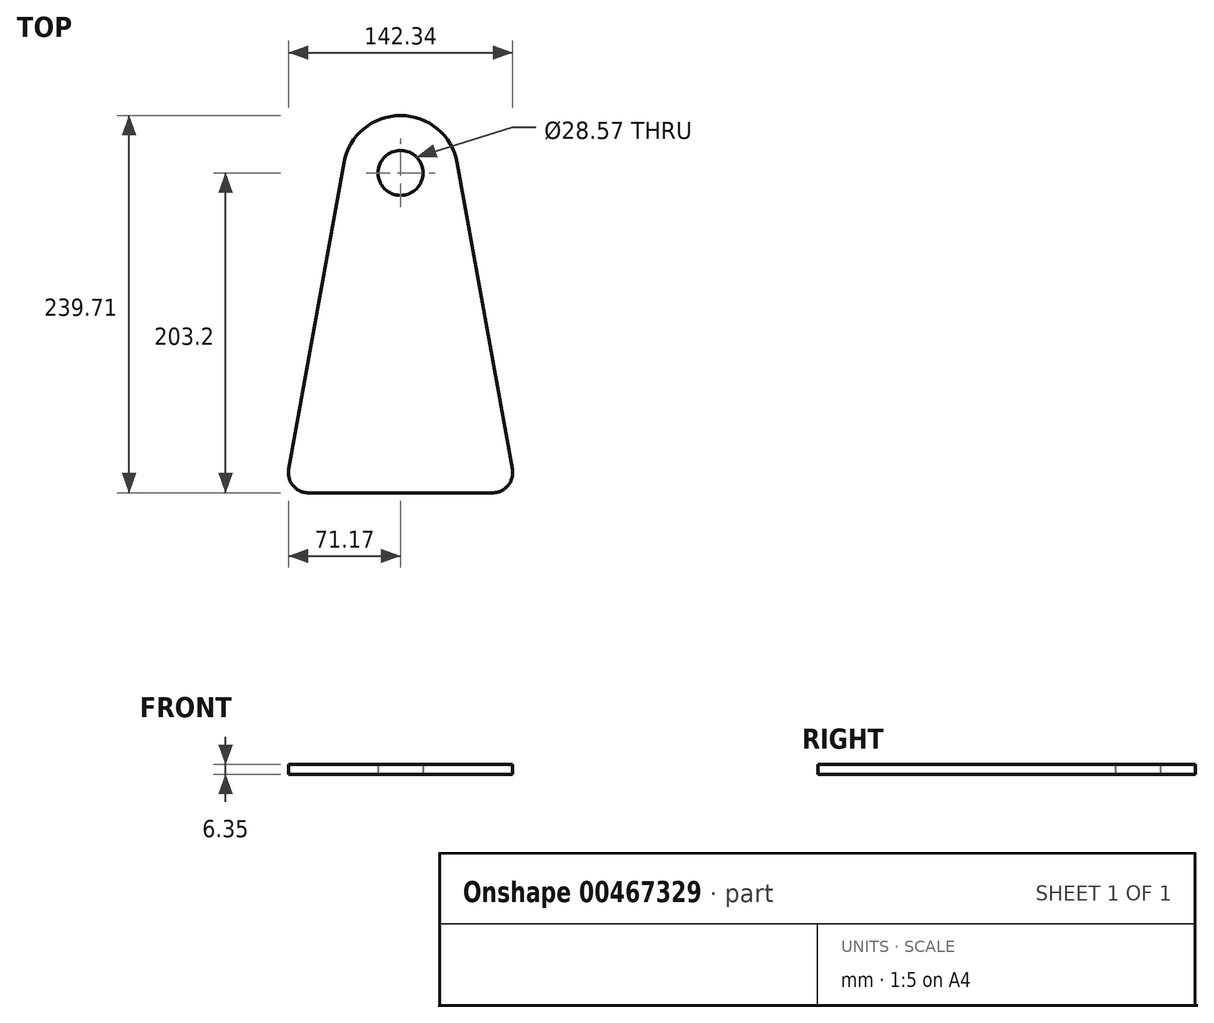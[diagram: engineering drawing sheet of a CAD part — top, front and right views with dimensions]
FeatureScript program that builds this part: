
annotation { "Feature Type Name" : "Feature", "Feature Type Description" : "" }
export const myFeature = defineFeature(function(context is Context, id is Id, definition is map)
    precondition{}
    {
        {
            var Q0;
            Q0=qCreatedBy(makeId("Top.planeOp"),FACE);
            var sketch = newSketch(context, id + "F0", { "sketchPlane" : qUnion([Q0])});
            skLineSegment(sketch, "E0", {"start": v(-58.47, 0) * mm, "end": v(58.47, 0) * mm});
            skCircle(sketch, "E1", {"center": v(0, 203.2) * mm, "radius": 14.29 * mm});
            skPoint(sketch, "E1.centerSnap0", {"position": v(0, 0) * mm});
            skLineSegment(sketch, "E2", {"start": v(-70.97, 14.95) * mm, "end": v(-35.38, 212.77) * mm});
            skLineSegment(sketch, "E3", {"start": v(35.38, 212.77) * mm, "end": v(70.97, 14.95) * mm});
            skPoint(sketch, "E4.visualSharp", {"position": v(-73.66, 0) * mm});
            skArc(sketch, "E4.filletArc", {"start": v(-70.97, 14.95) * mm, "mid": v(-68.21, 4.55) * mm, "end": v(-58.47, 0) * mm});
            skPoint(sketch, "E5.visualSharp", {"position": v(73.66, 0) * mm});
            skArc(sketch, "E5.filletArc", {"start": v(58.47, 0) * mm, "mid": v(68.21, 4.55) * mm, "end": v(70.97, 14.95) * mm});
            skArc(sketch, "E6.0", {"start": v(35.94, 209.67) * mm, "mid": v(0, 239.71) * mm, "end": v(-35.94, 209.67) * mm});
            skLineSegment(sketch, "E7", {"start": v(-8.73, 158.4) * mm, "end": v(0, 109.9) * mm, "construction": true});
            skLineSegment(sketch, "E8", {"start": v(0, 109.9) * mm, "end": v(83.25, 124.88) * mm, "construction": true});
            skLineSegment(sketch, "E9", {"start": v(83.25, 124.88) * mm, "end": v(74.6, 172.93) * mm, "construction": true});
            skLineSegment(sketch, "E10", {"start": v(74.6, 172.93) * mm, "end": v(-6.17, 158.4) * mm, "construction": true});
            skSolve(sketch);
        }
        {
            var Q0;
            Q0=makeQuery(id+"F0.imprint","IMPRINT",FACE,{"disambiguationData":[TD([[makeQuery(id+"F0.imprint","IMPRINT",EDGE,{"derivedFrom":sQuery(id+"F0.wireOp",EDGE,"E0")}),1.0]])]});
            extrude(context, id + "F1", {"entities" : qUnion([Q0]), "depth" : 6.35 * mm, "offsetDistance" : 25.4 * mm});
        }
    });
